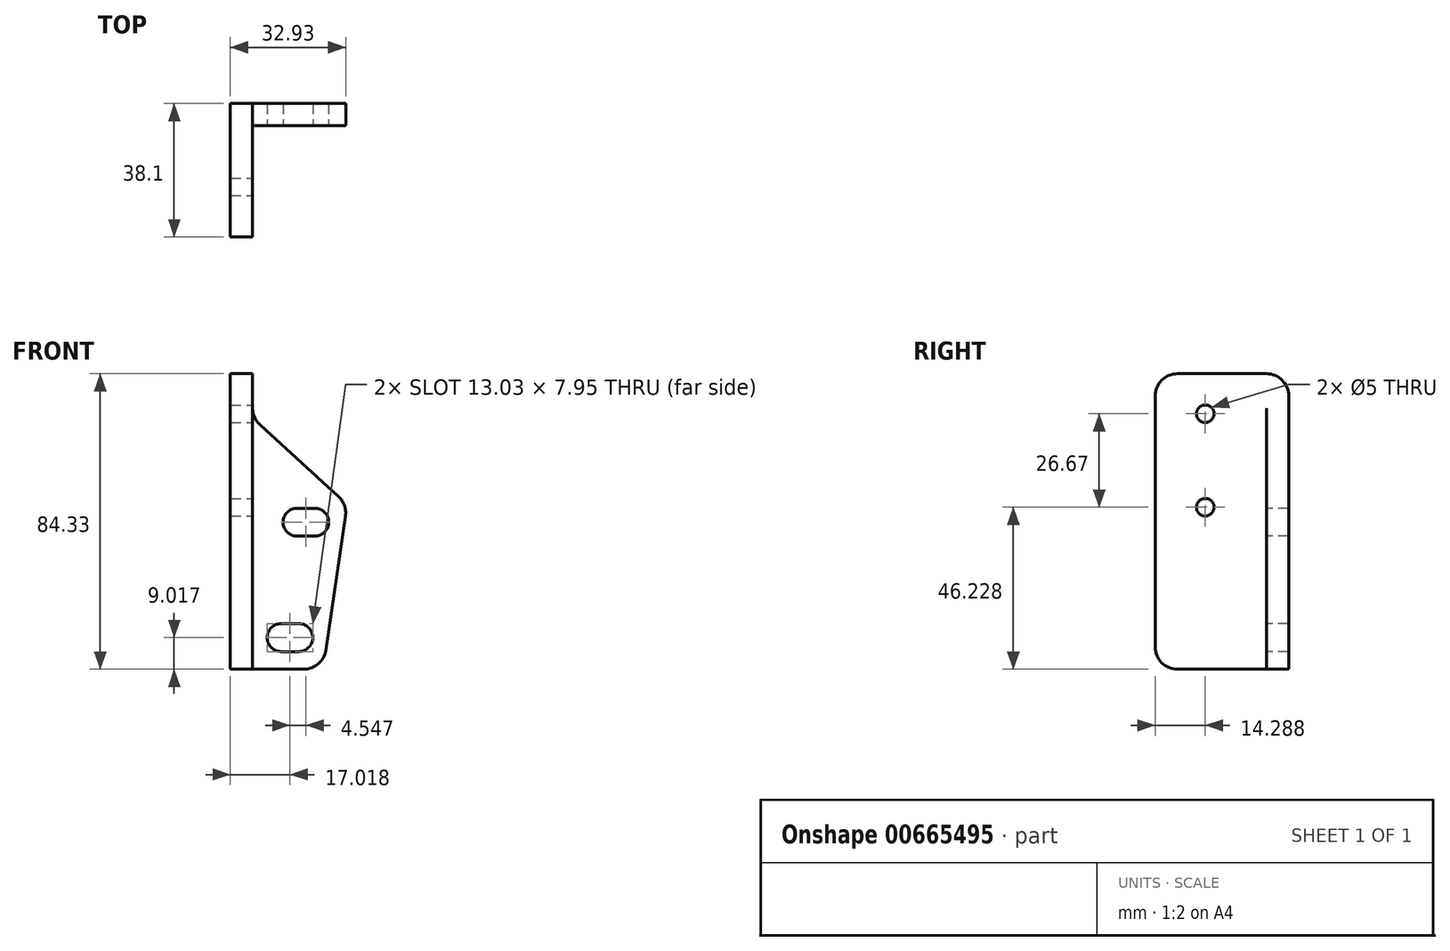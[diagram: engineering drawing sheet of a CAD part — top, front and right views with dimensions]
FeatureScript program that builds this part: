
annotation { "Feature Type Name" : "Feature", "Feature Type Description" : "" }
export const myFeature = defineFeature(function(context is Context, id is Id, definition is map)
    precondition{}
    {
        {
            var Q0;
            Q0=qCreatedBy(makeId("Front.planeOp"),FACE);
            var sketch = newSketch(context, id + "F0", { "sketchPlane" : qUnion([Q0])});
            skLineSegment(sketch, "E0", {"start": v(0, 0) * mm, "end": v(26.42, 0) * mm});
            skLineSegment(sketch, "E1", {"start": v(26.42, 0) * mm, "end": v(33.35, 47) * mm});
            skLineSegment(sketch, "E2", {"start": v(33.35, 46.99) * mm, "end": v(6.35, 71.63) * mm});
            skLineSegment(sketch, "E3", {"start": v(6.35, 71.63) * mm, "end": v(6.35, 84.33) * mm});
            skLineSegment(sketch, "E4", {"start": v(6.35, 84.33) * mm, "end": v(0, 84.33) * mm});
            skLineSegment(sketch, "E5", {"start": v(0, 84.33) * mm, "end": v(0, 0) * mm});
            skSolve(sketch);
        }
        {
            var Q0;
            Q0=makeQuery(id+"F0.imprint","IMPRINT",FACE,{"disambiguationData":[TD([[makeQuery(id+"F0.imprint","IMPRINT",EDGE,{"derivedFrom":sQuery(id+"F0.wireOp",EDGE,"E0")}),1.0]])]});
            extrude(context, id + "F1", {"entities" : qUnion([Q0]), "depth" : 6.35 * mm, "offsetDistance" : 25.4 * mm});
        }
        {
            var Q0;
            Q0=makeQuery(id+"F1.opExtrude","CAP_FACE",FACE,{"disambiguationData":[OSD([sQuery(id+"F0.wireOp",EDGE,"E0"),sQuery(id+"F0.wireOp",EDGE,"E1"),sQuery(id+"F0.wireOp",EDGE,"E2"),sQuery(id+"F0.wireOp",EDGE,"E3"),sQuery(id+"F0.wireOp",EDGE,"E4"),sQuery(id+"F0.wireOp",EDGE,"E5")])],"isStart":false});
            var sketch = newSketch(context, id + "F2", { "sketchPlane" : qUnion([Q0])});
            skLineSegment(sketch, "E6.bottom", {"start": v(0, 0) * mm, "end": v(6.35, 0) * mm});
            skLineSegment(sketch, "E6.top", {"start": v(0, 84.33) * mm, "end": v(6.35, 84.33) * mm});
            skLineSegment(sketch, "E6.left", {"start": v(0, 0) * mm, "end": v(0, 84.33) * mm});
            skLineSegment(sketch, "E6.right", {"start": v(6.35, 0) * mm, "end": v(6.35, 84.33) * mm});
            skSolve(sketch);
        }
        {
            var Q0;
            {var subQ2=sQuery(id+"F2.wireOp",EDGE,"E6.bottom");Q0=makeQuery(id+"F2.imprint","IMPRINT",FACE,{"disambiguationData":[TD([[makeQuery(id+"F2.imprint","IMPRINT",EDGE,{"derivedFrom":subQ2}),1.0]])]});}
            extrude(context, id + "F3", {"entities" : qUnion([Q0]), "operationType" : NewBodyOperationType.ADD, "depth" : 31.75 * mm, "offsetDistance" : 25.4 * mm});
        }
        {
            var Q0;
            Q0=makeQuery(id+"F1.opExtrude","CAP_FACE",FACE,{"disambiguationData":[OSD([sQuery(id+"F0.wireOp",EDGE,"E0"),sQuery(id+"F0.wireOp",EDGE,"E1"),sQuery(id+"F0.wireOp",EDGE,"E2"),sQuery(id+"F0.wireOp",EDGE,"E3"),sQuery(id+"F0.wireOp",EDGE,"E4"),sQuery(id+"F0.wireOp",EDGE,"E5")])],"isStart":false});
            var sketch = newSketch(context, id + "F4", { "sketchPlane" : qUnion([Q0])});
            skArc(sketch, "E7", {"start": v(14.48, 13) * mm, "mid": v(10.5, 9.02) * mm, "end": v(14.48, 5.04) * mm});
            skArc(sketch, "E8", {"start": v(19.56, 5.04) * mm, "mid": v(23.53, 9.02) * mm, "end": v(19.56, 13) * mm});
            skLineSegment(sketch, "E9.top", {"start": v(14.48, 13) * mm, "end": v(19.56, 13) * mm});
            skLineSegment(sketch, "E10.top", {"start": v(14.48, 5.04) * mm, "end": v(19.56, 5.04) * mm});
            skArc(sketch, "E11", {"start": v(19.02, 45.94) * mm, "mid": v(15.05, 41.96) * mm, "end": v(19.02, 37.99) * mm});
            skArc(sketch, "E12", {"start": v(24.1, 37.99) * mm, "mid": v(28.08, 41.96) * mm, "end": v(24.1, 45.94) * mm});
            skLineSegment(sketch, "E13.top", {"start": v(19.02, 45.94) * mm, "end": v(24.1, 45.94) * mm});
            skLineSegment(sketch, "E14.top", {"start": v(19.02, 37.99) * mm, "end": v(24.1, 37.99) * mm});
            skSolve(sketch);
        }
        {
            var Q0;
            Q0 = qSketchRegion(id + "F4", true);
            extrude(context, id + "F5", {"entities" : qUnion([Q0]), "operationType" : NewBodyOperationType.REMOVE, "oppositeDirection" : true, "depth" : 25.4 * mm, "offsetDistance" : 25.4 * mm});
        }
        {
            var Q0;
            Q0=makeQuery(id+"F3.boolean.opBoolean","MERGE",FACE,{"derivedFrom":[makeQuery(id+"F1.opExtrude","SWEPT_FACE",FACE,{"disambiguationData":[OSD([sQuery(id+"F0.wireOp",EDGE,"E3")])]}),makeQuery(id+"F3.opExtrude","SWEPT_FACE",FACE,{"disambiguationData":[OSD([sQuery(id+"F2.wireOp",EDGE,"E6.right")])]})]});
            var sketch = newSketch(context, id + "F6", { "sketchPlane" : qUnion([Q0])});
            skCircle(sketch, "E15", {"center": v(-23.81, 46.23) * mm, "radius": 2.5 * mm});
            skCircle(sketch, "E16", {"center": v(-23.81, 72.9) * mm, "radius": 2.5 * mm});
            skSolve(sketch);
        }
        {
            var Q0;
            Q0 = qSketchRegion(id + "F6", true);
            extrude(context, id + "F7", {"entities" : qUnion([Q0]), "operationType" : NewBodyOperationType.REMOVE, "oppositeDirection" : true, "depth" : 25.4 * mm, "offsetDistance" : 25.4 * mm});
        }
        {
            var Q0;
            Q0=makeQuery(id+"F1.opExtrude","SWEPT_EDGE",EDGE,{"disambiguationData":[OSD([sQuery(id+"F0.wireOp",EDGE,"E0"),sQuery(id+"F0.wireOp",EDGE,"E1")])]});
            var Q1;
            Q1=makeQuery(id+"F1.opExtrude","SWEPT_EDGE",EDGE,{"disambiguationData":[OSD([sQuery(id+"F0.wireOp",EDGE,"E1"),sQuery(id+"F0.wireOp",EDGE,"E2")])]});
            var Q2;
            Q2=makeQuery(id+"F1.opExtrude","SWEPT_EDGE",EDGE,{"disambiguationData":[OSD([sQuery(id+"F0.wireOp",EDGE,"E2"),sQuery(id+"F0.wireOp",EDGE,"E3")])]});
            var Q3;
            Q3=makeQuery(id+"F1.opExtrude","CAP_EDGE",EDGE,{"disambiguationData":[OSD([sQuery(id+"F0.wireOp",EDGE,"E4")])],"isStart":true});
            var Q4;
            Q4=makeQuery(id+"F3.opExtrude","CAP_EDGE",EDGE,{"disambiguationData":[OSD([sQuery(id+"F2.wireOp",EDGE,"E6.top")])],"isStart":false});
            var Q5;
            Q5=makeQuery(id+"F3.opExtrude","CAP_EDGE",EDGE,{"disambiguationData":[OSD([sQuery(id+"F2.wireOp",EDGE,"E6.bottom")])],"isStart":false});
            fillet(context, id + "F8", {"entities" : qUnion([Q0, Q1, Q2, Q3, Q4, Q5]), "radius" : 6.35 * mm, "tangentPropagation" : true, "allowEdgeOverflow" : false});
        }
    });
